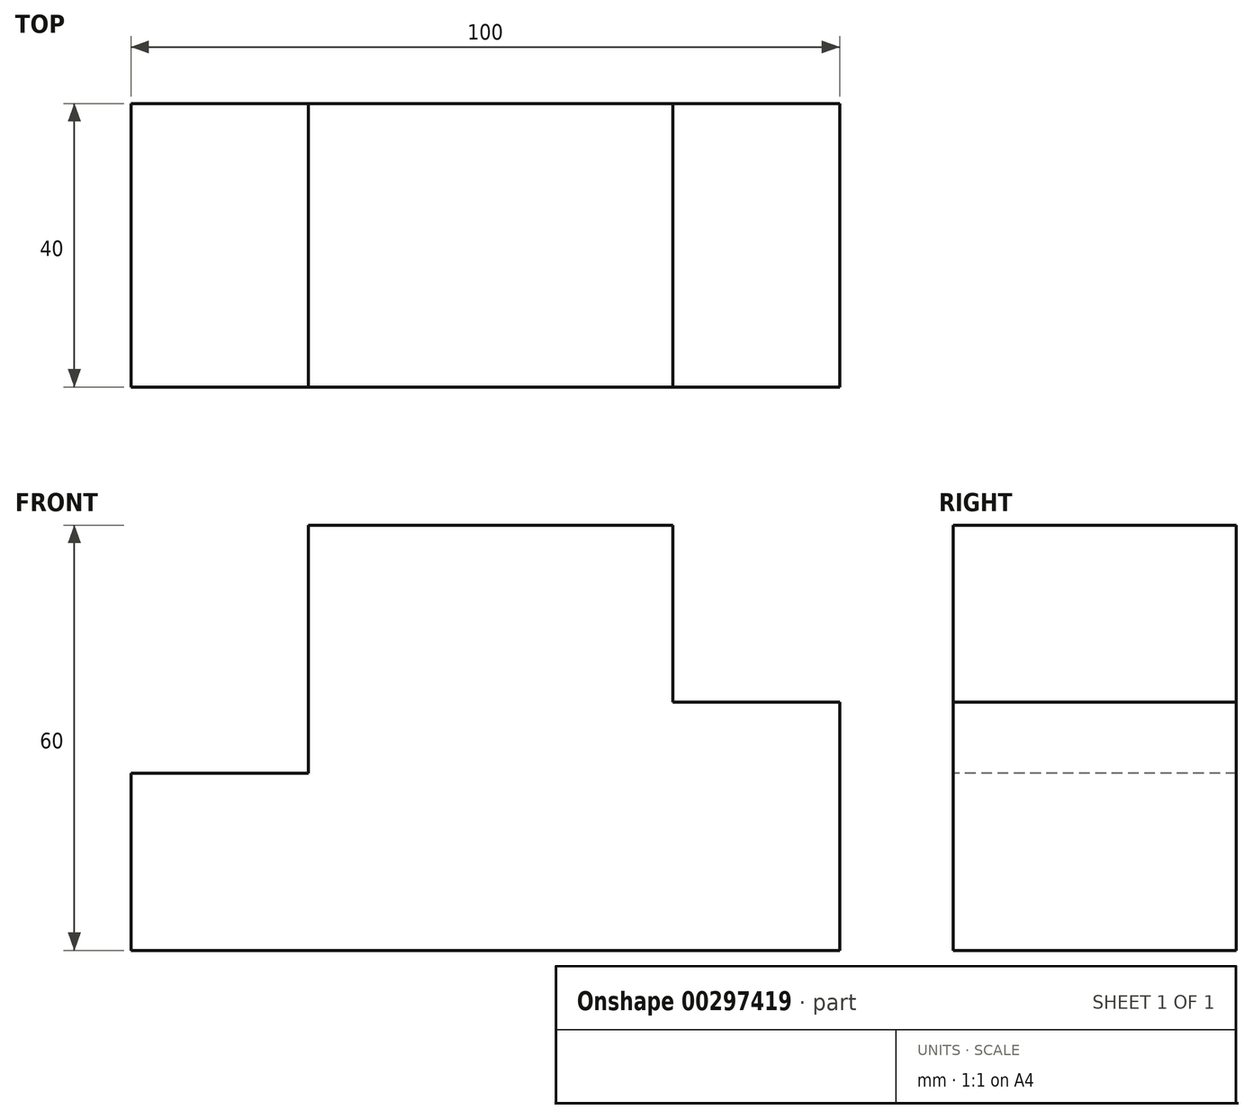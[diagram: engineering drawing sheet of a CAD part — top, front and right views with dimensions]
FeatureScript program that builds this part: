
annotation { "Feature Type Name" : "Feature", "Feature Type Description" : "" }
export const myFeature = defineFeature(function(context is Context, id is Id, definition is map)
    precondition{}
    {
        {
            var Q0;
            Q0=qCreatedBy(makeId("Front.planeOp"),FACE);
            var sketch = newSketch(context, id + "F0", { "sketchPlane" : qUnion([Q0])});
            skLineSegment(sketch, "E0.bottom", {"start": v(-46.09, 21.91) * mm, "end": v(53.91, 21.91) * mm});
            skLineSegment(sketch, "E0.top", {"start": v(-46.09, -38.09) * mm, "end": v(53.91, -38.09) * mm});
            skLineSegment(sketch, "E0.left", {"start": v(-46.09, 21.91) * mm, "end": v(-46.09, -38.09) * mm});
            skLineSegment(sketch, "E0.right", {"start": v(53.91, 21.91) * mm, "end": v(53.91, -38.09) * mm});
            skSolve(sketch);
        }
        {
            var Q0;
            Q0=makeQuery(id+"F0.imprint","IMPRINT",FACE,{"disambiguationData":[TD([[makeQuery(id+"F0.imprint","IMPRINT",EDGE,{"derivedFrom":sQuery(id+"F0.wireOp",EDGE,"E0.bottom")}),-1.0]])]});
            extrude(context, id + "F1", {"entities" : qUnion([Q0]), "depth" : 40 * mm});
        }
        {
            var Q0;
            Q0=makeQuery(id+"F1.opExtrude","CAP_FACE",FACE,{"disambiguationData":[OSD([sQuery(id+"F0.wireOp",EDGE,"E0.bottom"),sQuery(id+"F0.wireOp",EDGE,"E0.top"),sQuery(id+"F0.wireOp",EDGE,"E0.left"),sQuery(id+"F0.wireOp",EDGE,"E0.right")])],"isStart":false});
            var sketch = newSketch(context, id + "F2", { "sketchPlane" : qUnion([Q0])});
            skLineSegment(sketch, "E1.bottom", {"start": v(-46.09, 21.91) * mm, "end": v(-21.09, 21.91) * mm});
            skLineSegment(sketch, "E1.top", {"start": v(-46.09, -13.09) * mm, "end": v(-21.09, -13.09) * mm});
            skLineSegment(sketch, "E1.left", {"start": v(-46.09, 21.91) * mm, "end": v(-46.09, -13.09) * mm});
            skLineSegment(sketch, "E1.right", {"start": v(-21.09, 21.91) * mm, "end": v(-21.09, -13.09) * mm});
            skLineSegment(sketch, "E2.bottom", {"start": v(53.91, 21.91) * mm, "end": v(30.38, 21.91) * mm});
            skLineSegment(sketch, "E2.top", {"start": v(53.91, -3.09) * mm, "end": v(30.38, -3.09) * mm});
            skLineSegment(sketch, "E2.left", {"start": v(53.91, 21.91) * mm, "end": v(53.91, -3.09) * mm});
            skLineSegment(sketch, "E2.right", {"start": v(30.38, 21.91) * mm, "end": v(30.38, -3.09) * mm});
            skSolve(sketch);
        }
        {
            var Q0;
            Q0=makeQuery(id+"F2.imprint","IMPRINT",FACE,{"disambiguationData":[TD([[makeQuery(id+"F2.imprint","IMPRINT",EDGE,{"derivedFrom":sQuery(id+"F2.wireOp",EDGE,"E2.bottom")}),-1.0]])]});
            var Q1;
            Q1=makeQuery(id+"F2.imprint","IMPRINT",FACE,{"disambiguationData":[TD([[makeQuery(id+"F2.imprint","IMPRINT",EDGE,{"derivedFrom":sQuery(id+"F2.wireOp",EDGE,"E1.bottom")}),-1.0]])]});
            extrude(context, id + "F3", {"entities" : qUnion([Q0, Q1]), "operationType" : NewBodyOperationType.REMOVE, "endBound" : BoundingType.THROUGH_ALL, "oppositeDirection" : true, "depth" : 25.4 * mm});
        }
    });
